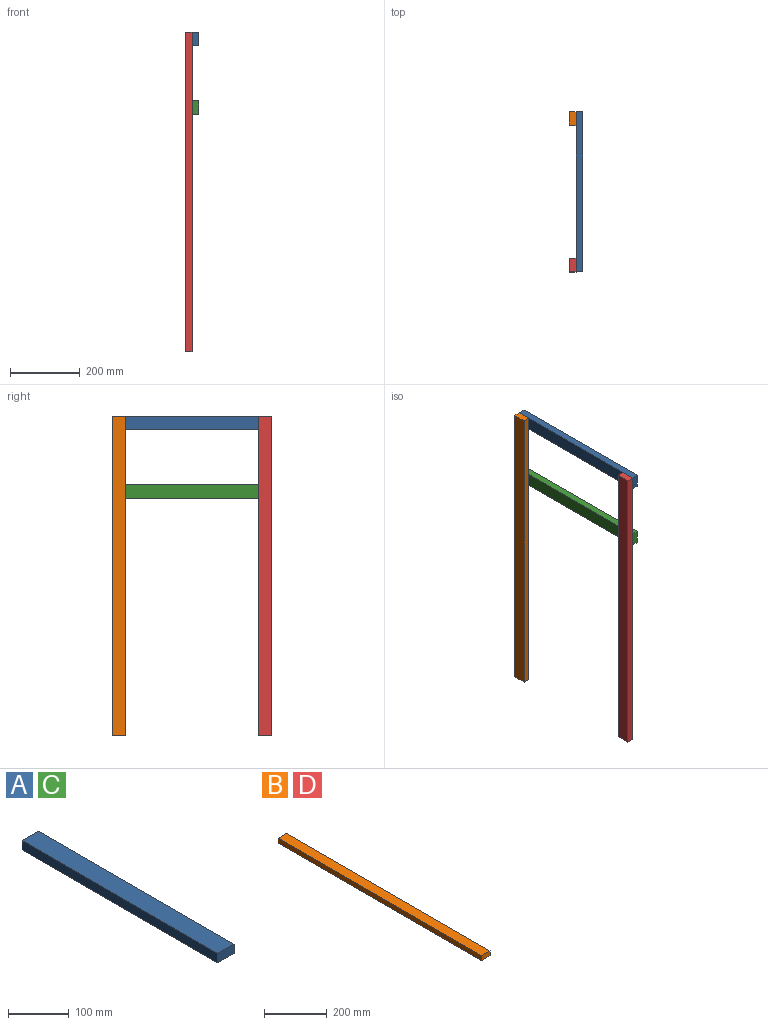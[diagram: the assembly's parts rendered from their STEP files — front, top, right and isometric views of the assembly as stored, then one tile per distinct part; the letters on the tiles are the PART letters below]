
ASSEMBLY  parts=4 mates=3
PART A: 6 faces, bbox 38.1x457.2x19.1 mm
  f0: plane 457.2x19.05mm, normal (-1,0,0), area 8709.7mm2, adj f1,f3,f4,f5
  f1: plane 38.1x19.05mm, normal (0,-1,0), area 725.8mm2, adj f0,f2,f4,f5
  f2: plane 457.2x19.05mm, normal (1,0,0), area 8709.7mm2, adj f1,f3,f4,f5
  f3: plane 38.1x19.05mm, normal (0,1,0), area 725.8mm2, adj f0,f2,f4,f5
  f4: plane 457.2x38.1mm, normal (0,0,1), area 17419.3mm2, adj f0,f1,f2,f3
  f5: plane 457.2x38.1mm, normal (0,0,-1), area 17419.3mm2, adj f0,f1,f2,f3
PART B: 6 faces, bbox 38.1x914.4x19.1 mm
  f0: plane 38.1x19.05mm, normal (0,-1,0), area 725.8mm2, adj f1,f3,f4,f5
  f1: plane 914.4x19.05mm, normal (1,0,0), area 17419.3mm2, adj f0,f2,f4,f5
  f2: plane 38.1x19.05mm, normal (0,1,0), area 725.8mm2, adj f1,f3,f4,f5
  f3: plane 914.4x19.05mm, normal (-1,0,0), area 17419.3mm2, adj f0,f2,f4,f5
  f4: plane 914.4x38.1mm, normal (0,0,1), area 34838.6mm2, adj f0,f1,f2,f3
  f5: plane 914.4x38.1mm, normal (0,0,-1), area 34838.6mm2, adj f0,f1,f2,f3
PART C: same geometry as A
PART D: same geometry as B
PLACE A rot(axis=(0,1,0),90deg) t=(9.53,209.55,783.97)mm
PLACE B rot(axis=(0.58,0.58,0.58),120deg) t=(-9.52,419.1,457.2)mm
PLACE C rot(axis=(0,1,0),90deg) t=(9.53,209.55,587.12)mm
PLACE D rot(axis=(0.58,0.58,0.58),120deg) t=(-9.52,0,457.2)mm
MATE fastened A.f5 <-> D.f4  axis (-1,0,0) through (9.53,-19.05,914.4)mm
MATE fastened C.f5 <-> D.f4  axis (-1,0,0) through (9.53,-19.05,717.55)mm
MATE fastened B.f4 <-> A.f5  axis (1,0,0) through (9.53,438.15,914.4)mm
